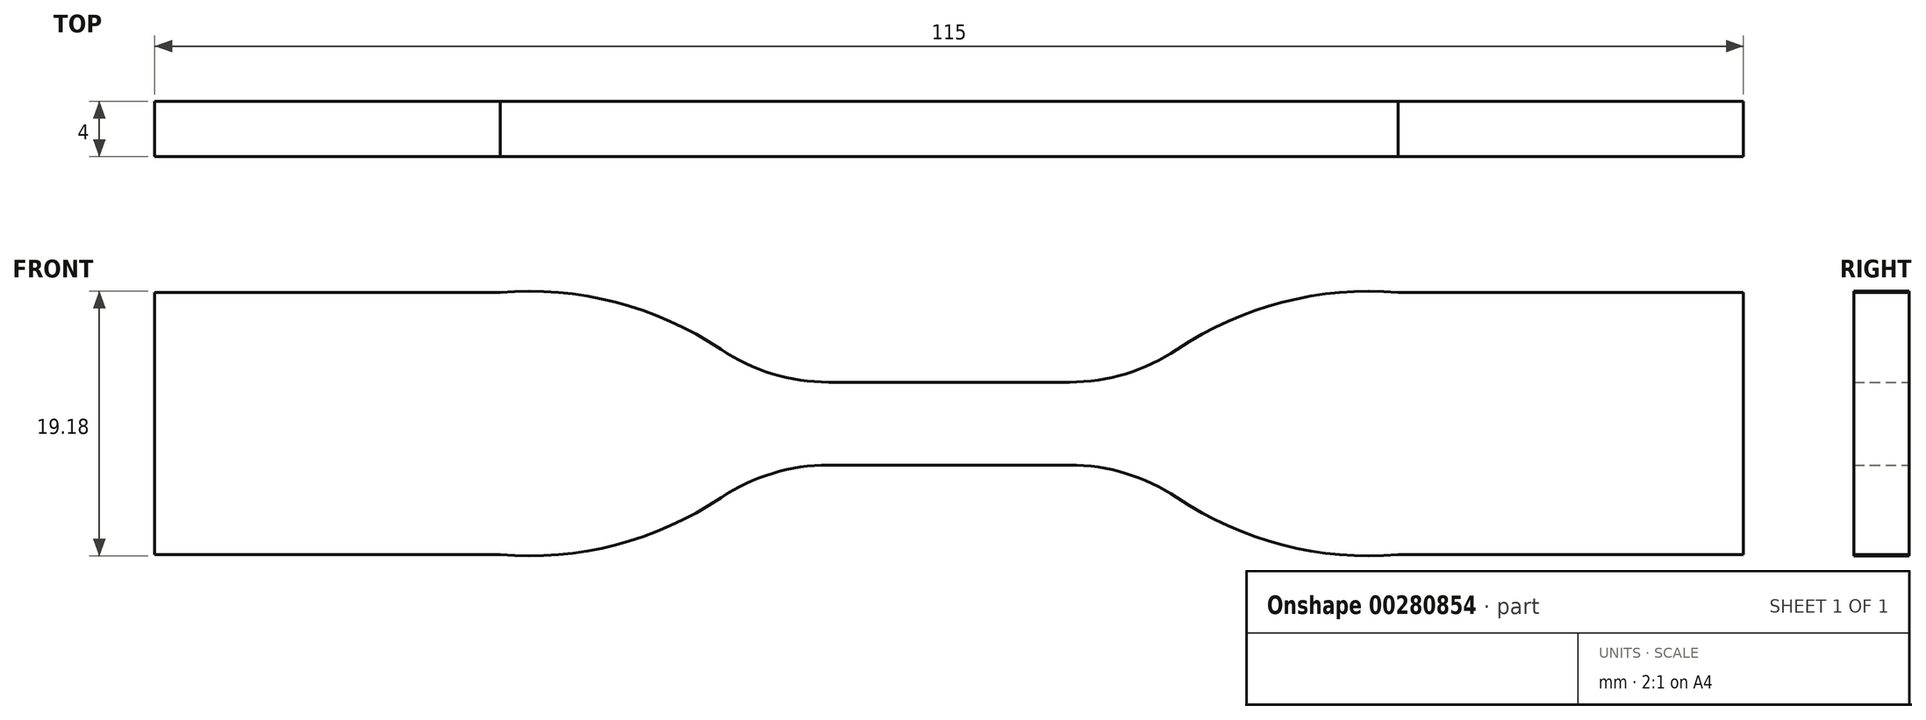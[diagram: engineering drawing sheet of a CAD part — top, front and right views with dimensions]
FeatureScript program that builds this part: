
annotation { "Feature Type Name" : "Feature", "Feature Type Description" : "" }
export const myFeature = defineFeature(function(context is Context, id is Id, definition is map)
    precondition{}
    {
        {
            var Q0;
            Q0=qCreatedBy(makeId("Front.planeOp"),FACE);
            var sketch = newSketch(context, id + "F0", { "sketchPlane" : qUnion([Q0])});
            skLineSegment(sketch, "E0", {"start": v(0, 3) * mm, "end": v(8.71, 3) * mm});
            skLineSegment(sketch, "E1", {"start": v(32.5, 9.5) * mm, "end": v(57.5, 9.5) * mm});
            skArc(sketch, "E2", {"start": v(8.71, 3) * mm, "mid": v(12.78, 3.6) * mm, "end": v(16.5, 5.36) * mm});
            skArc(sketch, "E3", {"start": v(16.5, 5.36) * mm, "mid": v(24.15, 8.8) * mm, "end": v(32.5, 9.5) * mm});
            skArc(sketch, "E4.MirrorCS", {"start": v(8.71, -3) * mm, "mid": v(12.78, -3.6) * mm, "end": v(16.5, -5.36) * mm});
            skLineSegment(sketch, "E5.MirrorCS", {"start": v(32.5, -9.5) * mm, "end": v(57.5, -9.5) * mm});
            skLineSegment(sketch, "E6.MirrorCS", {"start": v(0, -3) * mm, "end": v(8.71, -3) * mm});
            skArc(sketch, "E7.MirrorCS", {"start": v(16.5, -5.36) * mm, "mid": v(24.15, -8.8) * mm, "end": v(32.5, -9.5) * mm});
            skLineSegment(sketch, "E8.MirrorCS", {"start": v(0, -3) * mm, "end": v(-8.71, -3) * mm});
            skLineSegment(sketch, "E9.MirrorCS", {"start": v(-32.5, -9.5) * mm, "end": v(-57.5, -9.5) * mm});
            skArc(sketch, "E10.MirrorCS", {"start": v(-8.71, -3) * mm, "mid": v(-12.78, -3.6) * mm, "end": v(-16.5, -5.36) * mm});
            skArc(sketch, "E11.MirrorCS", {"start": v(-16.5, 5.36) * mm, "mid": v(-24.15, 8.8) * mm, "end": v(-32.5, 9.5) * mm});
            skLineSegment(sketch, "E12.MirrorCS", {"start": v(0, 3) * mm, "end": v(-8.71, 3) * mm});
            skLineSegment(sketch, "E13.MirrorCS", {"start": v(-32.5, 9.5) * mm, "end": v(-57.5, 9.5) * mm});
            skArc(sketch, "E14.MirrorCS", {"start": v(-16.5, -5.36) * mm, "mid": v(-24.15, -8.8) * mm, "end": v(-32.5, -9.5) * mm});
            skArc(sketch, "E15.MirrorCS", {"start": v(-8.71, 3) * mm, "mid": v(-12.78, 3.6) * mm, "end": v(-16.5, 5.36) * mm});
            skLineSegment(sketch, "E16", {"start": v(-57.5, 9.5) * mm, "end": v(-57.5, -9.5) * mm});
            skLineSegment(sketch, "E17", {"start": v(57.5, 9.5) * mm, "end": v(57.5, -9.5) * mm});
            skSolve(sketch);
        }
        {
            var Q0;
            Q0=makeQuery(id+"F0.imprint","IMPRINT",FACE,{"disambiguationData":[TD([[makeQuery(id+"F0.imprint","IMPRINT",EDGE,{"derivedFrom":sQuery(id+"F0.wireOp",EDGE,"E0")}),-1.0]])]});
            extrude(context, id + "F1", {"entities" : qUnion([Q0]), "endBound" : BoundingType.SYMMETRIC, "depth" : 4 * mm});
        }
    });
